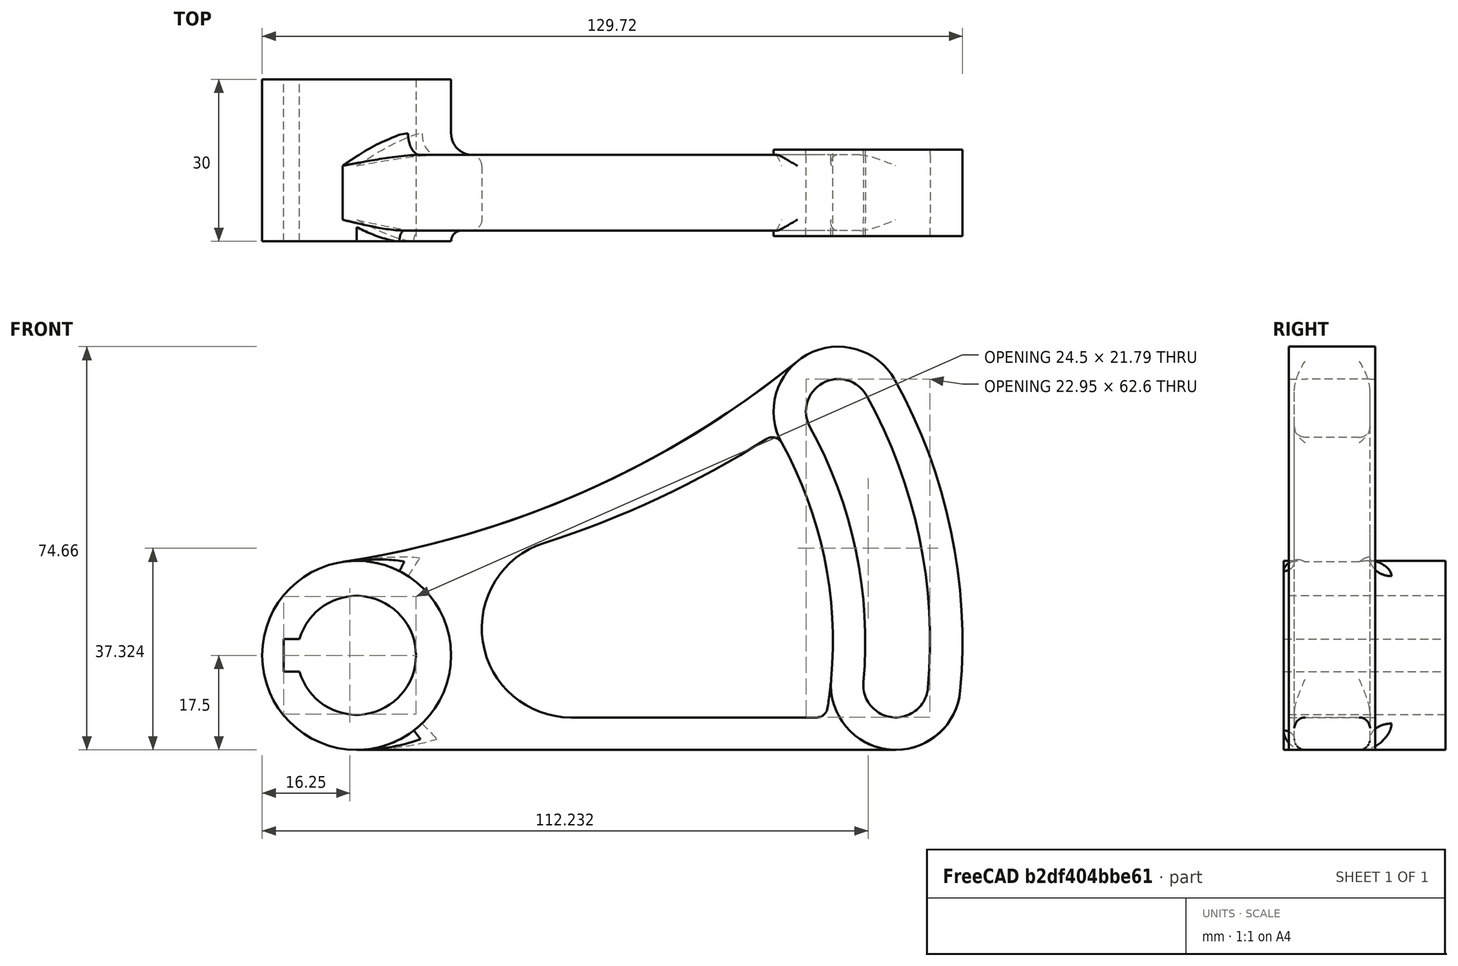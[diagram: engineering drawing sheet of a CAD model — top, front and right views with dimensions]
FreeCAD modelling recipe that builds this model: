
FCSTD DOCUMENT  (FreeCAD 1.0R39319 (Git))
Label: Mania2008
License: All rights reserved
LicenseURL: https://en.wikipedia.org/wiki/All_rights_reserved
objects: Sketcher::SketchObject×6, PartDesign::Fillet×3, PartDesign::Pad×2, PartDesign::Pocket×2, PartDesign::Revolution×2, PartDesign::Body×1
note: 40 computed .brp shape members not serialized (recipe doc carries the construction recipe); baked Part::Feature solids carry a one-line shape summary decoded from their .brp

FEATURE [Sketcher::SketchObject] Sketch
  ArcFitTolerance = 1e-06
  AttachmentSupport = -> [XZ_Plane]
  FullyConstrained = true
  MakeInternals = false
  MapMode = 5
  Placement = pos=(0,0,0) rot=(1,0,0;1.5708rad)
  sketch-geometry (9):
    g0: LineSegment [constr] StartX=0 StartY=0 StartZ=0 EndX=89.2215 EndY=45.1612 EndZ=0
    g1: LineSegment [constr] StartX=0 StartY=0 StartZ=0 EndX=99.8486 EndY=-5.5 EndZ=0
    g2: ArcOfCircle CenterX=0 CenterY=0 CenterZ=0 NormalX=0 NormalY=0 NormalZ=1 AngleXU=0 Radius=17.5 StartAngle=1.72001 EndAngle=4.71239
    g3: LineSegment StartX=0 StartY=-17.5 StartZ=0 EndX=99.8486 EndY=-17.5 EndZ=0
    g4: ArcOfCircle CenterX=-28.6175 CenterY=190.361 CenterZ=0 NormalX=0 NormalY=0 NormalZ=1 AngleXU=0 Radius=175 StartAngle=4.8616 EndAngle=5.39414
    g5: ArcOfCircle [constr] CenterX=0 CenterY=0 CenterZ=0 NormalX=0 NormalY=0 NormalZ=1 AngleXU=0 Radius=100 StartAngle=6.22816 EndAngle=6.75176
    g6: ArcOfCircle CenterX=89.2215 CenterY=45.1612 CenterZ=0 NormalX=0 NormalY=0 NormalZ=1 AngleXU=0 Radius=12 StartAngle=0.505298 EndAngle=2.25255
    g7: ArcOfCircle CenterX=99.8486 CenterY=-5.5 CenterZ=0 NormalX=0 NormalY=0 NormalZ=1 AngleXU=0 Radius=12 StartAngle=4.71239 EndAngle=6.19143
    g8: ArcOfCircle CenterX=12.2188 CenterY=2.56314 CenterZ=0 NormalX=0 NormalY=0 NormalZ=1 AngleXU=0 Radius=100 StartAngle=6.19143 EndAngle=6.78848
  constraints (22):
    c: Coincident(g0,g-1)
    c: Coincident(g1,g0)
    c: Angle(g1,g0) = 0.523599
    c: Coincident(g2,g0)
    c: Diameter(g2) = 35
    c: Radius(g4) = 175
    c: Tangent(g4,g2) = 1.5708
    c: Tangent(g3,g2) = -1.5708
    c: Coincident(g5,g0)
    c: Coincident(g5,g1)
    c: Coincident(g5,g0)
    c: Radius(g5) = 100
    c: Coincident(g6,g0)
    c: Radius(g6) = 12
    c: Coincident(g7,g1)
    c: Equal(g6,g7)
    c: Tangent(g8,g6) = -1.5708
    c: Tangent(g4,g6) = 1.5708
    c: Tangent(g8,g7) = -1.5708
    c: Tangent(g3,g7) = -1.5708
    c: Equal(g8,g5)
    c: Horizontal(g3)
FEATURE [PartDesign::Pad] Pad
  Direction = (0,-1,2e-16)
  Length = 14
  Length2 = 10
  Midplane = true
  Placement = pos=(0,0,0) rot=(1,0,0;1.5708rad)
  Profile = -> Sketch
  ReferenceAxis = -> Sketch [N_Axis]
  Refine = true
  Suppressed = false
  Type = 0
FEATURE [Sketcher::SketchObject] Sketch001
  ArcFitTolerance = 1e-06
  AttachmentOffset = pos=(0,0,-7) rot=(0,0,1;0rad)
  AttachmentSupport = -> [Pad]
  ExternalGeometry = -> [Pad]
  FullyConstrained = true
  MakeInternals = false
  MapMode = 5
  Placement = pos=(0,2.7e-15,-1.6e-15) rot=(1,0,0;1.5708rad)
  expr: .AttachmentOffset.Base.z = -<<Pad>>.Length / 2
  sketch-geometry (8):
    g0: ArcOfCircle CenterX=89.2215 CenterY=45.1612 CenterZ=0 NormalX=0 NormalY=0 NormalZ=1 AngleXU=0 Radius=6 StartAngle=0.505299 EndAngle=3.64689
    g1: ArcOfCircle CenterX=99.8486 CenterY=-5.5 CenterZ=0 NormalX=0 NormalY=0 NormalZ=1 AngleXU=0 Radius=6 StartAngle=3.04984 EndAngle=6.19143
    g2: ArcOfCircle CenterX=12.2188 CenterY=2.56314 CenterZ=0 NormalX=0 NormalY=0 NormalZ=1 AngleXU=0 Radius=94 StartAngle=6.19143 EndAngle=6.78848
    g3: ArcOfCircle CenterX=12.2188 CenterY=2.56314 CenterZ=0 NormalX=0 NormalY=0 NormalZ=1 AngleXU=0 Radius=82 StartAngle=6.19143 EndAngle=6.78848
    g4: ArcOfCircle CenterX=89.2215 CenterY=45.1612 CenterZ=0 NormalX=0 NormalY=0 NormalZ=1 AngleXU=0 Radius=12 StartAngle=0.505298 EndAngle=3.64689
    g5: ArcOfCircle CenterX=12.2188 CenterY=2.56314 CenterZ=0 NormalX=0 NormalY=0 NormalZ=1 AngleXU=0 Radius=76 StartAngle=6.19143 EndAngle=6.78848
    g6: ArcOfCircle CenterX=99.8486 CenterY=-5.5 CenterZ=0 NormalX=0 NormalY=0 NormalZ=1 AngleXU=0 Radius=12 StartAngle=3.04984 EndAngle=6.19143
    g7: ArcOfCircle CenterX=12.2189 CenterY=2.56316 CenterZ=0 NormalX=0 NormalY=0 NormalZ=1 AngleXU=0 Radius=99.9999 StartAngle=6.19143 EndAngle=6.78848
  constraints (20):
    c: Coincident(g0,g-5)
    c: Distance(g0,g-5) = 6
    c: Coincident(g1,g-4)
    c: Coincident(g2,g-3)
    c: Coincident(g2,g0)
    c: Coincident(g3,g2)
    c: Coincident(g3,g0)
    c: Distance(g2,g-3) = 6
    c: Tangent(g3,g1) = 1.5708
    c: Tangent(g2,g1) = -1.5708
    c: Coincident(g4,g0)
    c: Coincident(g4,g-5)
    c: Coincident(g5,g2)
    c: Coincident(g6,g1)
    c: Coincident(g6,g5)
    c: PointOnObject(g6,g-3)
    c: Equal(g4,g6)
    c: Tangent(g5,g4) = 1.5708
    c: Coincident(g7,g4)
    c: Tangent(g7,g6) = -1.5708
FEATURE [Sketcher::SketchObject] Sketch002
  ArcFitTolerance = 1e-06
  FullyConstrained = true
  MakeInternals = false
  MapMode = 5
  Placement = pos=(0,0,0) rot=(1,0,0;1.5708rad)
  sketch-geometry (11):
    g0: ArcOfCircle CenterX=-18.2294 CenterY=187.602 CenterZ=0 NormalX=0 NormalY=0 NormalZ=1 AngleXU=0 Radius=175 StartAngle=5.01976 EndAngle=5.28028
    g1: ArcOfCircle CenterX=12.2188 CenterY=2.56314 CenterZ=0 NormalX=0 NormalY=0 NormalZ=1 AngleXU=0 Radius=76 StartAngle=6.11944 EndAngle=6.78848
    g2: ArcOfCircle CenterX=76.971 CenterY=38.3842 CenterZ=0 NormalX=0 NormalY=0 NormalZ=1 AngleXU=0 Radius=2 StartAngle=0.505298 EndAngle=2.13869
    g3: ArcOfCircle CenterX=85.229 CenterY=-9.5 CenterZ=0 NormalX=0 NormalY=0 NormalZ=1 AngleXU=0 Radius=2 StartAngle=4.71239 EndAngle=6.11944
    g4: LineSegment StartX=85.229 StartY=-11.5 StartZ=0 EndX=39.7209 EndY=-11.5 EndZ=0
    g5: ArcOfCircle CenterX=39.7209 CenterY=5.03929 CenterZ=0 NormalX=0 NormalY=0 NormalZ=1 AngleXU=0 Radius=16.5393 StartAngle=1.87816 EndAngle=4.71239
    g6: Circle [constr] CenterX=0 CenterY=0 CenterZ=0 NormalX=0 NormalY=0 NormalZ=1 AngleXU=0 Radius=17.5
    g7: ArcOfCircle CenterX=12.2188 CenterY=2.56313 CenterZ=0 NormalX=0 NormalY=0 NormalZ=1 AngleXU=0 Radius=82 StartAngle=6.19143 EndAngle=6.78848
    g8: ArcOfCircle CenterX=99.8486 CenterY=-5.5 CenterZ=0 NormalX=0 NormalY=0 NormalZ=1 AngleXU=0 Radius=6 StartAngle=3.04984 EndAngle=6.19143
    g9: ArcOfCircle CenterX=12.2189 CenterY=2.56314 CenterZ=0 NormalX=0 NormalY=0 NormalZ=1 AngleXU=0 Radius=94 StartAngle=6.19143 EndAngle=6.78848
    g10: ArcOfCircle CenterX=89.2215 CenterY=45.1612 CenterZ=0 NormalX=0 NormalY=0 NormalZ=1 AngleXU=0 Radius=6 StartAngle=0.505299 EndAngle=3.64689
  constraints (25):
    c: Coincident(g1,g-9)
    c: Coincident(g1,g-9)
    c: Radius(g0) = 175
    c: Radius(g2) = 2
    c: Tangent(g2,g1) = -1.5708
    c: Tangent(g2,g0) = 1.5708
    c: Equal(g2,g3)
    c: Tangent(g3,g1) = -1.5708
    c: Distance(g0,g-3) = 6
    c: Horizontal(g4)
    c: Distance(g-4,g4) = 6
    c: Tangent(g4,g3) = 1.5708
    c: Tangent(g5,g0) = 1.5708
    c: Tangent(g5,g4) = 1.5708
    c: Diameter(g6) = 35
    c: Coincident(g6,g-1)
    c: Distance(g6,g5) = 6
    c: Tangent(g-7,g7) = 1.5708
    c: Coincident(g7,g-8)
    c: Tangent(g7,g8) = 1.5708
    c: Coincident(g8,g-8)
    c: Tangent(g8,g9) = -1.5708
    c: Coincident(g9,g-7)
    c: Tangent(g9,g10) = -1.5708
    c: Coincident(g10,g7)
FEATURE [PartDesign::Pocket] Pocket
  BaseFeature = -> Pad
  Direction = (0,1,-2e-16)
  Length = 5
  Length2 = 5
  Midplane = true
  Placement = pos=(0,0,0) rot=(1,0,0;1.5708rad)
  Profile = -> Sketch002
  ReferenceAxis = -> Sketch002 [N_Axis]
  Refine = true
  Suppressed = false
  Type = 1
FEATURE [PartDesign::Fillet] Fillet
  Base = -> Pocket [Edge14,Edge6,Edge27,Edge33,Edge7]
  BaseFeature = -> Pocket
  Placement = pos=(0,0,0) rot=(1,0,0;1.5708rad)
  Radius = 2
  Refine = true
  SupportTransform = false
  Suppressed = false
  UseAllEdges = false
FEATURE [PartDesign::Pad] Pad001
  BaseFeature = -> Fillet
  Direction = (0,-1,2e-16)
  Length = 16
  Length2 = 10
  Midplane = true
  Placement = pos=(0,0,0) rot=(1,0,0;1.5708rad)
  Profile = -> Sketch001
  ReferenceAxis = -> Sketch001 [N_Axis]
  Refine = true
  Suppressed = false
  Type = 0
FEATURE [Sketcher::SketchObject] Sketch003
  ArcFitTolerance = 1e-06
  AttachmentSupport = -> [YZ_Plane]
  FullyConstrained = true
  MakeInternals = false
  MapMode = 5
  Placement = pos=(0,0,0) rot=(0.57735,0.57735,0.57735;2.0944rad)
  sketch-geometry (4):
    g0: LineSegment StartX=-9 StartY=0 StartZ=0 EndX=-9 EndY=-17.5 EndZ=0
    g1: LineSegment StartX=-9 StartY=-17.5 StartZ=0 EndX=21 EndY=-17.5 EndZ=0
    g2: LineSegment StartX=21 StartY=-17.5 StartZ=0 EndX=21 EndY=0 EndZ=0
    g3: LineSegment StartX=-9 StartY=0 StartZ=0 EndX=21 EndY=0 EndZ=0
  constraints (12):
    c: PointOnObject(g0,g-1)
    c: Vertical(g0)
    c: Coincident(g1,g0)
    c: Horizontal(g1)
    c: DistanceX(g1,g1) = 30
    c: Distance(g-2,g0) = 9
    c: Coincident(g2,g1)
    c: PointOnObject(g2,g-1)
    c: Vertical(g2)
    c: Coincident(g3,g0)
    c: Coincident(g3,g2)
    c: DistanceY(g2,g2) = 17.5
FEATURE [PartDesign::Revolution] Revolution
  Angle = 180
  Angle2 = 60
  Axis = (1e-16,1,-1e-16)
  Base = (0,0,0)
  BaseFeature = -> Pad001
  Placement = pos=(0,0,0) rot=(1,0,0;1.5708rad)
  Profile = -> Sketch003
  ReferenceAxis = -> Y_Axis
  Refine = true
  Suppressed = false
  Type = 0
FEATURE [Sketcher::SketchObject] Sketch004
  ArcFitTolerance = 1e-06
  AttachmentSupport = -> [YZ_Plane]
  ExternalGeometry = -> [Revolution]
  FullyConstrained = true
  MakeInternals = false
  MapMode = 5
  Placement = pos=(0,0,0) rot=(0.57735,0.57735,0.57735;2.0944rad)
  sketch-geometry (4):
    g0: LineSegment StartX=21 StartY=17.5 StartZ=0 EndX=21 EndY=0 EndZ=0
    g1: LineSegment StartX=-9 StartY=17.5 StartZ=0 EndX=-9 EndY=0 EndZ=0
    g2: LineSegment StartX=-9 StartY=0 StartZ=0 EndX=21 EndY=0 EndZ=0
    g3: LineSegment StartX=21 StartY=17.5 StartZ=0 EndX=-9 EndY=17.5 EndZ=0
  constraints (12):
    c: DistanceX(g1,g0) = 30
    c: Distance(g1,g-2) = 9
    c: Vertical(g0)
    c: Vertical(g1)
    c: Coincident(g2,g1)
    c: Coincident(g2,g0)
    c: Horizontal(g2)
    c: PointOnObject(g0,g-1)
    c: DistanceY(g0,g0) = 17.5
    c: Coincident(g0,g3)
    c: Horizontal(g3)
    c: Coincident(g3,g1)
FEATURE [PartDesign::Revolution] Revolution001
  Angle = 180
  Angle2 = 60
  Axis = (1e-16,1,-1e-16)
  Base = (0,0,0)
  BaseFeature = -> Revolution
  Placement = pos=(0,0,0) rot=(1,0,0;1.5708rad)
  Profile = -> Sketch004
  ReferenceAxis = -> Y_Axis
  Refine = true
  Suppressed = false
  Type = 0
FEATURE [PartDesign::Fillet] Fillet001
  Base = -> Revolution001 [Edge3]
  BaseFeature = -> Revolution001
  Placement = pos=(0,0,0) rot=(1,0,0;1.5708rad)
  Radius = 3.99
  Refine = true
  SupportTransform = false
  Suppressed = false
  UseAllEdges = false
FEATURE [PartDesign::Fillet] Fillet002
  Base = -> Fillet001 [Edge35]
  BaseFeature = -> Fillet001
  Placement = pos=(0,0,0) rot=(1,0,0;1.5708rad)
  Radius = 1.99
  Refine = true
  SupportTransform = false
  Suppressed = false
  UseAllEdges = false
FEATURE [Sketcher::SketchObject] Sketch005
  ArcFitTolerance = 1e-06
  AttachmentSupport = -> [Fillet002]
  FullyConstrained = true
  MakeInternals = false
  MapMode = 5
  Placement = pos=(-2.1e-15,-9,3.1e-15) rot=(1,0,0;1.5708rad)
  sketch-geometry (5):
    g0: ArcOfCircle CenterX=0 CenterY=0 CenterZ=0 NormalX=0 NormalY=0 NormalZ=1 AngleXU=0 Radius=11 StartAngle=3.41782 EndAngle=9.14855
    g1: LineSegment StartX=-13.5 StartY=3 StartZ=0 EndX=-13.5 EndY=-3 EndZ=0
    g2: LineSegment StartX=-13.5 StartY=-3 StartZ=0 EndX=-10.583 EndY=-3 EndZ=0
    g3: LineSegment StartX=-10.583 StartY=3 StartZ=0 EndX=-13.5 EndY=3 EndZ=0
    g4: GeomPoint X=11 Y=0 Z=0
  constraints (13):
    c: Diameter(g0) = 22
    c: Coincident(g0,g-1)
    c: Coincident(g1,g2)
    c: Coincident(g3,g1)
    c: Horizontal(g2)
    c: Horizontal(g3)
    c: Symmetric(g1,g1,g-1)
    c: DistanceY(g1,g1) = 6
    c: PointOnObject(g4,g0)
    c: PointOnObject(g4,g-1)
    c: Distance(g4,g1) = 24.5
    c: Coincident(g0,g3)
    c: Coincident(g0,g2)
FEATURE [PartDesign::Pocket] Pocket001
  BaseFeature = -> Fillet002
  Direction = (0,1,-2e-16)
  Length = 5
  Length2 = 5
  Placement = pos=(0,0,0) rot=(1,0,0;1.5708rad)
  Profile = -> Sketch005
  ReferenceAxis = -> Sketch005 [N_Axis]
  Refine = true
  Suppressed = false
  Type = 1
FEATURE [PartDesign::Body] Body
  AllowCompound = false
  Group = -> [Sketch,Pad,Sketch001,Sketch002,Pocket,Fillet,Pad001,Sketch003,Revolution,Sketch004,Revolution001,Fillet001,Fillet002,Sketch005,Pocket001]
  Origin = -> Origin
  Tip = -> Pocket001
